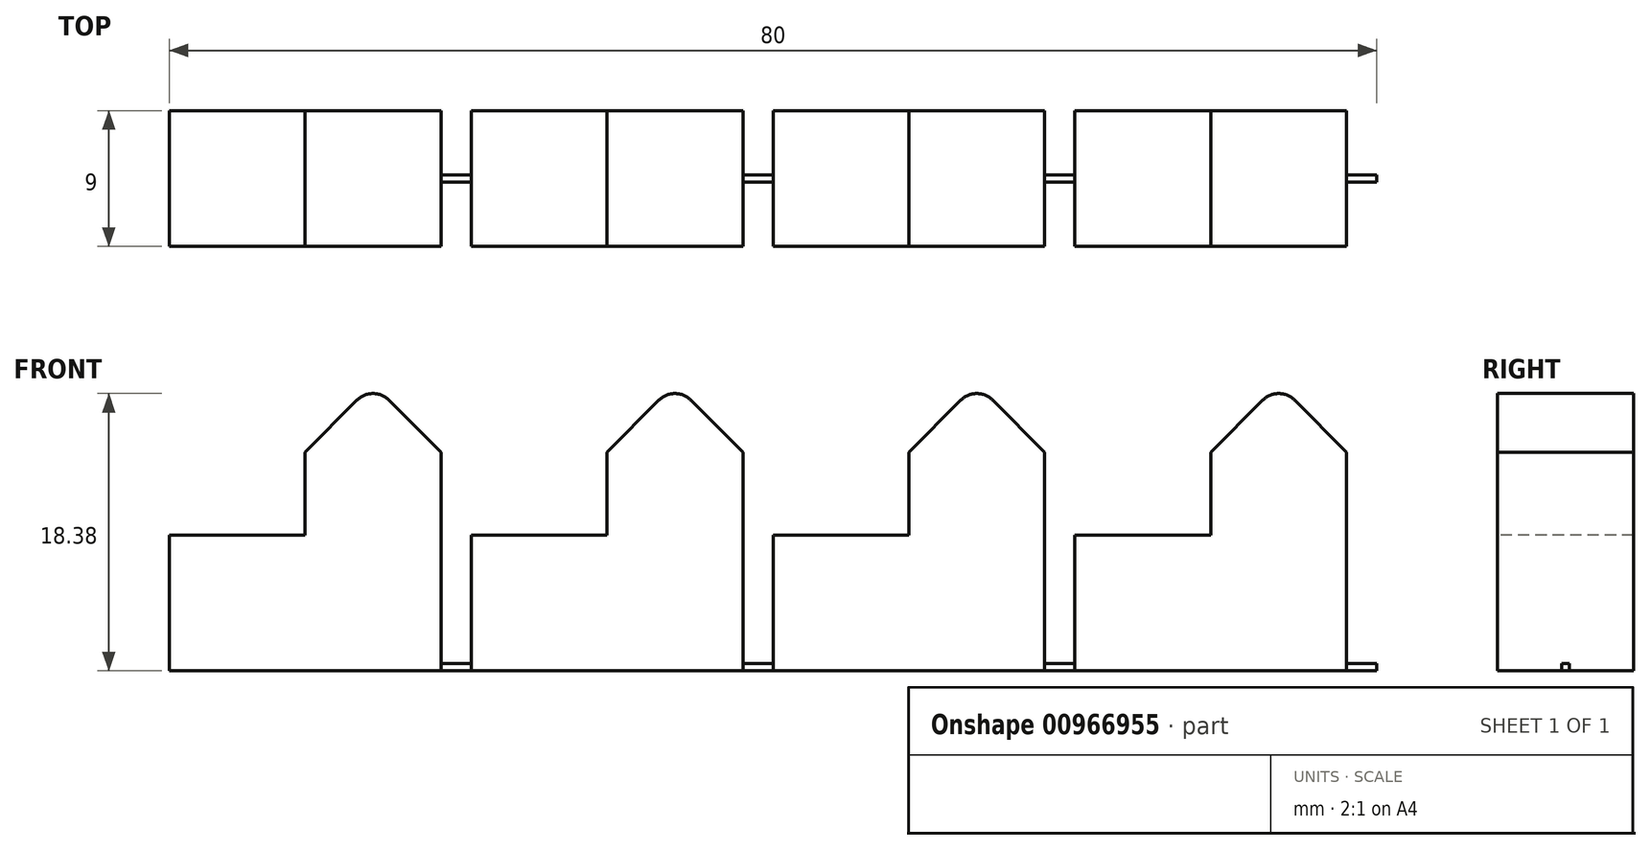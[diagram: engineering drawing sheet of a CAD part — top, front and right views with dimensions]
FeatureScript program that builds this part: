
annotation { "Feature Type Name" : "Feature", "Feature Type Description" : "" }
export const myFeature = defineFeature(function(context is Context, id is Id, definition is map)
    precondition{}
    {
        {
            var Q0;
            Q0=qCreatedBy(makeId("Front.planeOp"),FACE);
            var sketch = newSketch(context, id + "F0", { "sketchPlane" : qUnion([Q0])});
            skLineSegment(sketch, "E0.bottom", {"start": v(9, -4.5) * mm, "end": v(-9, -4.5) * mm});
            skLineSegment(sketch, "E0.left", {"start": v(9, -4) * mm, "end": v(9, 4.5) * mm});
            skLineSegment(sketch, "E0.right", {"start": v(-9, -4.5) * mm, "end": v(-9, 4.5) * mm});
            skPoint(sketch, "E0.middle", {"position": v(0, 0) * mm});
            skLineSegment(sketch, "E1.left", {"start": v(9, 4.5) * mm, "end": v(9, 10) * mm});
            skLineSegment(sketch, "E1.right", {"start": v(0, 4.5) * mm, "end": v(0, 10) * mm});
            skLineSegment(sketch, "E2", {"start": v(0, 10) * mm, "end": v(3.44, 13.44) * mm});
            skLineSegment(sketch, "E3", {"start": v(5.56, 13.44) * mm, "end": v(9, 10) * mm});
            skArc(sketch, "E4.filletArc", {"start": v(5.56, 13.44) * mm, "mid": v(4.5, 13.88) * mm, "end": v(3.44, 13.44) * mm});
            skLineSegment(sketch, "E5", {"start": v(0, 4.5) * mm, "end": v(-9, 4.5) * mm});
            skLineSegment(sketch, "E6.direction1", {"start": v(-9, -4.5) * mm, "end": v(11, -4.5) * mm, "construction": true});
            skLineSegment(sketch, "E7.bottom", {"start": v(9, -4.5) * mm, "end": v(11, -4.5) * mm});
            skLineSegment(sketch, "E7.top", {"start": v(9, -4) * mm, "end": v(11, -4) * mm});
            skLineSegment(sketch, "E7.right", {"start": v(11, -4.5) * mm, "end": v(11, -4) * mm});
            skLineSegment(sketch, "E8.1.0.0", {"start": v(11, -4.5) * mm, "end": v(11, 4.5) * mm});
            skPoint(sketch, "E8.1.0.1", {"position": v(20, 0) * mm});
            skLineSegment(sketch, "E8.1.0.2", {"start": v(20, 4.5) * mm, "end": v(20, 10) * mm});
            skArc(sketch, "E8.1.0.3", {"start": v(25.56, 13.44) * mm, "mid": v(24.5, 13.88) * mm, "end": v(23.44, 13.44) * mm});
            skLineSegment(sketch, "E8.1.0.4", {"start": v(25.56, 13.44) * mm, "end": v(29, 10) * mm});
            skLineSegment(sketch, "E8.1.0.5", {"start": v(11, -4.5) * mm, "end": v(31, -4.5) * mm, "construction": true});
            skLineSegment(sketch, "E8.1.0.6", {"start": v(29, -4) * mm, "end": v(31, -4) * mm});
            skLineSegment(sketch, "E8.1.0.7", {"start": v(29, 4.5) * mm, "end": v(29, 10) * mm});
            skLineSegment(sketch, "E8.1.0.8", {"start": v(20, 10) * mm, "end": v(23.44, 13.44) * mm});
            skLineSegment(sketch, "E8.1.0.9", {"start": v(29, -4) * mm, "end": v(29, 4.5) * mm});
            skLineSegment(sketch, "E8.1.0.10", {"start": v(20, 4.5) * mm, "end": v(11, 4.5) * mm});
            skLineSegment(sketch, "E8.1.0.11", {"start": v(29, -4.5) * mm, "end": v(11, -4.5) * mm});
            skLineSegment(sketch, "E8.1.0.12", {"start": v(29, -4.5) * mm, "end": v(31, -4.5) * mm});
            skLineSegment(sketch, "E8.1.0.13", {"start": v(31, -4.5) * mm, "end": v(31, -4) * mm});
            skLineSegment(sketch, "E8.2.0.0", {"start": v(31, -4.5) * mm, "end": v(31, 4.5) * mm});
            skPoint(sketch, "E8.2.0.1", {"position": v(40, 0) * mm});
            skLineSegment(sketch, "E8.2.0.2", {"start": v(40, 4.5) * mm, "end": v(40, 10) * mm});
            skArc(sketch, "E8.2.0.3", {"start": v(45.56, 13.44) * mm, "mid": v(44.5, 13.88) * mm, "end": v(43.44, 13.44) * mm});
            skLineSegment(sketch, "E8.2.0.4", {"start": v(45.56, 13.44) * mm, "end": v(49, 10) * mm});
            skLineSegment(sketch, "E8.2.0.5", {"start": v(31, -4.5) * mm, "end": v(51, -4.5) * mm, "construction": true});
            skLineSegment(sketch, "E8.2.0.6", {"start": v(49, -4) * mm, "end": v(51, -4) * mm});
            skLineSegment(sketch, "E8.2.0.7", {"start": v(49, 4.5) * mm, "end": v(49, 10) * mm});
            skLineSegment(sketch, "E8.2.0.8", {"start": v(40, 10) * mm, "end": v(43.44, 13.44) * mm});
            skLineSegment(sketch, "E8.2.0.9", {"start": v(49, -4) * mm, "end": v(49, 4.5) * mm});
            skLineSegment(sketch, "E8.2.0.10", {"start": v(40, 4.5) * mm, "end": v(31, 4.5) * mm});
            skLineSegment(sketch, "E8.2.0.11", {"start": v(49, -4.5) * mm, "end": v(31, -4.5) * mm});
            skLineSegment(sketch, "E8.2.0.12", {"start": v(49, -4.5) * mm, "end": v(51, -4.5) * mm});
            skLineSegment(sketch, "E8.2.0.13", {"start": v(51, -4.5) * mm, "end": v(51, -4) * mm});
            skLineSegment(sketch, "E8.3.0.0", {"start": v(51, -4.5) * mm, "end": v(51, 4.5) * mm});
            skPoint(sketch, "E8.3.0.1", {"position": v(60, 0) * mm});
            skLineSegment(sketch, "E8.3.0.2", {"start": v(60, 4.5) * mm, "end": v(60, 10) * mm});
            skArc(sketch, "E8.3.0.3", {"start": v(65.56, 13.44) * mm, "mid": v(64.5, 13.88) * mm, "end": v(63.44, 13.44) * mm});
            skLineSegment(sketch, "E8.3.0.4", {"start": v(65.56, 13.44) * mm, "end": v(69, 10) * mm});
            skLineSegment(sketch, "E8.3.0.5", {"start": v(51, -4.5) * mm, "end": v(71, -4.5) * mm, "construction": true});
            skLineSegment(sketch, "E8.3.0.6", {"start": v(69, -4) * mm, "end": v(71, -4) * mm});
            skLineSegment(sketch, "E8.3.0.7", {"start": v(69, 4.5) * mm, "end": v(69, 10) * mm});
            skLineSegment(sketch, "E8.3.0.8", {"start": v(60, 10) * mm, "end": v(63.44, 13.44) * mm});
            skLineSegment(sketch, "E8.3.0.9", {"start": v(69, -4) * mm, "end": v(69, 4.5) * mm});
            skLineSegment(sketch, "E8.3.0.10", {"start": v(60, 4.5) * mm, "end": v(51, 4.5) * mm});
            skLineSegment(sketch, "E8.3.0.11", {"start": v(69, -4.5) * mm, "end": v(51, -4.5) * mm});
            skLineSegment(sketch, "E8.3.0.12", {"start": v(69, -4.5) * mm, "end": v(71, -4.5) * mm});
            skLineSegment(sketch, "E8.3.0.13", {"start": v(71, -4.5) * mm, "end": v(71, -4) * mm});
            skSolve(sketch);
        }
        {
            var Q0;
            Q0=makeQuery(id+"F0.imprint","IMPRINT",FACE,{"disambiguationData":[TD([[makeQuery(id+"F0.imprint","IMPRINT",EDGE,{"derivedFrom":sQuery(id+"F0.wireOp",EDGE,"E0.bottom")}),-1.0]])]});
            var Q1;
            Q1=makeQuery(id+"F0.imprint","IMPRINT",FACE,{"disambiguationData":[TD([[makeQuery(id+"F0.imprint","IMPRINT",EDGE,{"derivedFrom":sQuery(id+"F0.wireOp",EDGE,"E6.1.0.0")}),-1.0]])]});
            var Q2;
            Q2=makeQuery(id+"F0.imprint","IMPRINT",FACE,{"disambiguationData":[TD([[makeQuery(id+"F0.imprint","IMPRINT",EDGE,{"derivedFrom":sQuery(id+"F0.wireOp",EDGE,"E6.2.0.0")}),-1.0]])]});
            var Q3;
            Q3=makeQuery(id+"F0.imprint","IMPRINT",FACE,{"disambiguationData":[TD([[makeQuery(id+"F0.imprint","IMPRINT",EDGE,{"derivedFrom":sQuery(id+"F0.wireOp",EDGE,"E6.3.0.0")}),-1.0]])]});
            var Q4;
            Q4=makeQuery(id+"F0.imprint","IMPRINT",FACE,{"disambiguationData":[TD([[makeQuery(id+"F0.imprint","IMPRINT",EDGE,{"derivedFrom":sQuery(id+"F0.wireOp",EDGE,"E8.1.0.2")}),-1.0]])]});
            var Q5;
            Q5=makeQuery(id+"F0.imprint","IMPRINT",FACE,{"disambiguationData":[TD([[makeQuery(id+"F0.imprint","IMPRINT",EDGE,{"derivedFrom":sQuery(id+"F0.wireOp",EDGE,"E8.2.0.2")}),-1.0]])]});
            var Q6;
            Q6=makeQuery(id+"F0.imprint","IMPRINT",FACE,{"disambiguationData":[TD([[makeQuery(id+"F0.imprint","IMPRINT",EDGE,{"derivedFrom":sQuery(id+"F0.wireOp",EDGE,"E8.3.0.2")}),-1.0]])]});
            extrude(context, id + "F1", {"entities" : qUnion([Q0, Q1, Q2, Q3, Q4, Q5, Q6]), "oppositeDirection" : true, "depth" : 9 * mm, "offsetDistance" : 25 * mm});
        }
        {
            var Q0;
            Q0=makeQuery(id+"F1.opExtrude","SWEPT_FACE",FACE,{"disambiguationData":[OSD([sQuery(id+"F0.wireOp",EDGE,"E0.bottom"),sQuery(id+"F0.wireOp",EDGE,"E7.bottom"),sQuery(id+"F0.wireOp",EDGE,"E8.1.0.11"),sQuery(id+"F0.wireOp",EDGE,"E8.1.0.12"),sQuery(id+"F0.wireOp",EDGE,"E8.2.0.11"),sQuery(id+"F0.wireOp",EDGE,"E8.2.0.12"),sQuery(id+"F0.wireOp",EDGE,"E8.3.0.11"),sQuery(id+"F0.wireOp",EDGE,"E8.3.0.12")])]});
            var sketch = newSketch(context, id + "F2", { "sketchPlane" : qUnion([Q0])});
            skPoint(sketch, "E9", {"position": v(9, 0) * mm});
            skLineSegment(sketch, "E10.bottom", {"start": v(9, 0) * mm, "end": v(11, 0) * mm});
            skLineSegment(sketch, "E10.top", {"start": v(9, -4.25) * mm, "end": v(11, -4.25) * mm});
            skLineSegment(sketch, "E10.left", {"start": v(9, 0) * mm, "end": v(9, -4.25) * mm});
            skLineSegment(sketch, "E10.right", {"start": v(11, 0) * mm, "end": v(11, -4.25) * mm});
            skLineSegment(sketch, "E11.0.1.0", {"start": v(9, -4.75) * mm, "end": v(11, -4.75) * mm});
            skPoint(sketch, "E11.0.1.1", {"position": v(9, -4.75) * mm});
            skLineSegment(sketch, "E11.0.1.2", {"start": v(11, -4.75) * mm, "end": v(11, -9) * mm});
            skLineSegment(sketch, "E11.0.1.3", {"start": v(9, -9) * mm, "end": v(11, -9) * mm});
            skLineSegment(sketch, "E11.0.1.4", {"start": v(9, -4.75) * mm, "end": v(9, -9) * mm});
            skLineSegment(sketch, "E11.1.0.0", {"start": v(29, 0) * mm, "end": v(31, 0) * mm});
            skPoint(sketch, "E11.1.0.1", {"position": v(29, 0) * mm});
            skLineSegment(sketch, "E11.1.0.2", {"start": v(31, 0) * mm, "end": v(31, -4.25) * mm});
            skLineSegment(sketch, "E11.1.0.3", {"start": v(29, -4.25) * mm, "end": v(31, -4.25) * mm});
            skLineSegment(sketch, "E11.1.0.4", {"start": v(29, 0) * mm, "end": v(29, -4.25) * mm});
            skLineSegment(sketch, "E11.1.1.0", {"start": v(29, -4.75) * mm, "end": v(31, -4.75) * mm});
            skPoint(sketch, "E11.1.1.1", {"position": v(29, -4.75) * mm});
            skLineSegment(sketch, "E11.1.1.2", {"start": v(31, -4.75) * mm, "end": v(31, -9) * mm});
            skLineSegment(sketch, "E11.1.1.3", {"start": v(29, -9) * mm, "end": v(31, -9) * mm});
            skLineSegment(sketch, "E11.1.1.4", {"start": v(29, -4.75) * mm, "end": v(29, -9) * mm});
            skLineSegment(sketch, "E11.2.0.0", {"start": v(49, 0) * mm, "end": v(51, 0) * mm});
            skPoint(sketch, "E11.2.0.1", {"position": v(49, 0) * mm});
            skLineSegment(sketch, "E11.2.0.2", {"start": v(51, 0) * mm, "end": v(51, -4.25) * mm});
            skLineSegment(sketch, "E11.2.0.3", {"start": v(49, -4.25) * mm, "end": v(51, -4.25) * mm});
            skLineSegment(sketch, "E11.2.0.4", {"start": v(49, 0) * mm, "end": v(49, -4.25) * mm});
            skLineSegment(sketch, "E11.2.1.0", {"start": v(49, -4.75) * mm, "end": v(51, -4.75) * mm});
            skPoint(sketch, "E11.2.1.1", {"position": v(49, -4.75) * mm});
            skLineSegment(sketch, "E11.2.1.2", {"start": v(51, -4.75) * mm, "end": v(51, -9) * mm});
            skLineSegment(sketch, "E11.2.1.3", {"start": v(49, -9) * mm, "end": v(51, -9) * mm});
            skLineSegment(sketch, "E11.2.1.4", {"start": v(49, -4.75) * mm, "end": v(49, -9) * mm});
            skLineSegment(sketch, "E11.3.0.0", {"start": v(69, 0) * mm, "end": v(71, 0) * mm});
            skPoint(sketch, "E11.3.0.1", {"position": v(69, 0) * mm});
            skLineSegment(sketch, "E11.3.0.2", {"start": v(71, 0) * mm, "end": v(71, -4.25) * mm});
            skLineSegment(sketch, "E11.3.0.3", {"start": v(69, -4.25) * mm, "end": v(71, -4.25) * mm});
            skLineSegment(sketch, "E11.3.0.4", {"start": v(69, 0) * mm, "end": v(69, -4.25) * mm});
            skLineSegment(sketch, "E11.3.1.0", {"start": v(69, -4.75) * mm, "end": v(71, -4.75) * mm});
            skPoint(sketch, "E11.3.1.1", {"position": v(69, -4.75) * mm});
            skLineSegment(sketch, "E11.3.1.2", {"start": v(71, -4.75) * mm, "end": v(71, -9) * mm});
            skLineSegment(sketch, "E11.3.1.3", {"start": v(69, -9) * mm, "end": v(71, -9) * mm});
            skLineSegment(sketch, "E11.3.1.4", {"start": v(69, -4.75) * mm, "end": v(69, -9) * mm});
            skLineSegment(sketch, "E11.direction1", {"start": v(9, -4.25) * mm, "end": v(29, -4.25) * mm, "construction": true});
            skLineSegment(sketch, "E11.direction2", {"start": v(9, -4.25) * mm, "end": v(9, -9) * mm, "construction": true});
            skSolve(sketch);
        }
        {
            var Q0;
            Q0 = qSketchRegion(id + "F2", true);
            extrude(context, id + "F3", {"entities" : qUnion([Q0]), "operationType" : NewBodyOperationType.REMOVE, "endBound" : BoundingType.THROUGH_ALL, "oppositeDirection" : true, "depth" : 25 * mm, "offsetDistance" : 25 * mm});
        }
    });
